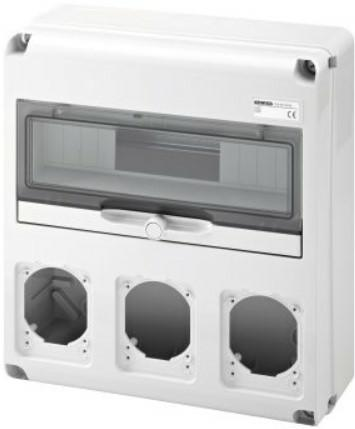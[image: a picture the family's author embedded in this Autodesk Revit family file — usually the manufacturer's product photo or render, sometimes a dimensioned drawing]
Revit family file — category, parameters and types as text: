
# Revit family: Building-QuadriIEC309-GEWISS-68QDIN-QUADRI-PRESE-14MOD_3PRESE
name_source: partatom
category: Apparecchi elettrici
units: mm (PartAtom-declared; Revit-internal decimal feet)

## family parameters
Condiviso = No
Host = Superficie
Mantenere orientamento annotazione = Sì
Punto di calcolo locali = Sì
Quota connettore circolare = Usa diametro
Taglio con vuoti quando caricato = No
Tipo di parte = Normale

## types (1)
- GW68005N - Q-DIN 14M 3FLANGE PR.16/32A IP65
    Catalogo = BUILDING
    Catalogo Serie = 68 QDIN
    Classe isolamento = II
    Codice EAN = 8011564744769
    Codice Electrocod = 2242
    Colore = Grigio RAL 7035
    Conformità normativa = EN 60208 - EN 60670-1 - IEC 60670-24
    Descrizione = Q-DIN 14M 3FLANGE PR.16/32A IP65
    Glow Wire Test = 650°C
    Grado di protezione = IP65
    IDF = 64fd8844-c356-49a2-a1c7-5f6e02194f4d
    IDT = 63e6b50c-c9b0-4c82-844b-021dcb4b6831
    Immagine tipo = GW68005N.jpg
    Modello = GW68005N
    N. coperchi ciechi in dotazione = 1 IEC 16/32 A
    N. flange in dotazione = 1 IB 16/32 A
    N. mod. EN 50022 = 14
    N. prese alloggiabili = 3 IEC 309 16/32 A IP44/67
    POMELLO = bianco
    PRESA = rosso
    Potenza dissipabile A (W) = 24
    Potenza dissipabile B (W) = 64
    Produttore = GEWISS S.p.A.
    Prospetto di default = 1219 mm
    Resistenza agli urti = IK08
    SEO = Quadretto
    STRUTTURA = RAL - 7035
    STRUTTURA ALTA = Poche
    Scheda Tecnica = https://www.gewiss.com
    Spostamento_S = 1000 mm  [stored 3.28084 ft]
    Temperatura di funzionamento = -25 ÷ +40 °C
    Temperatura di utilizzo = -25 +40 °C
    Termopressione con biglia = 70 °C
    Tipo versione = Vuoto
    Tipologia di installazione = Da parete
    URL = https://www.gewiss.com
    VETRO = Vetro
    Versione file RFA = 21.5

note: [stored X ft] marks values corroborated as IEEE doubles in the binary element streams (Revit-internal decimal feet)

## geometry (parser evidence)
native form markers: Sweep x4
no freeform markers — native parametric forms only
